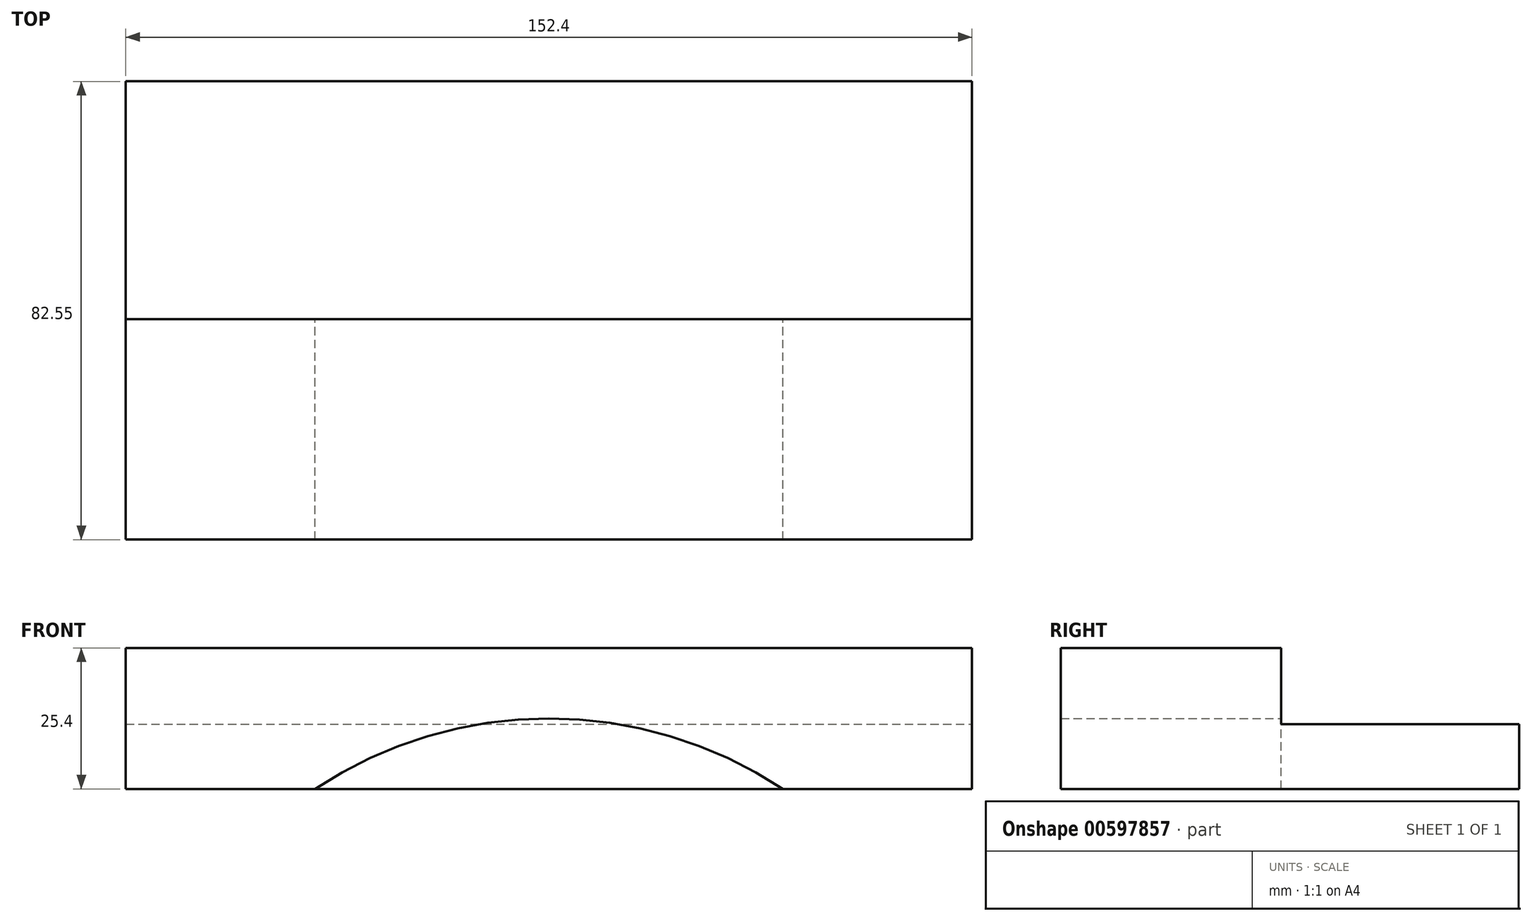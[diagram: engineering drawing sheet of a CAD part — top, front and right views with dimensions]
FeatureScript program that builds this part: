
annotation { "Feature Type Name" : "Feature", "Feature Type Description" : "" }
export const myFeature = defineFeature(function(context is Context, id is Id, definition is map)
    precondition{}
    {
        {
            var Q0;
            Q0=qCreatedBy(makeId("Front.planeOp"),FACE);
            var sketch = newSketch(context, id + "F0", { "sketchPlane" : qUnion([Q0])});
            skLineSegment(sketch, "E0.bottom", {"start": v(0, 0) * mm, "end": v(34.08, 0) * mm});
            skLineSegment(sketch, "E0.top", {"start": v(0, 25.4) * mm, "end": v(152.4, 25.4) * mm});
            skLineSegment(sketch, "E0.left", {"start": v(0, 0) * mm, "end": v(0, 25.4) * mm});
            skLineSegment(sketch, "E0.right", {"start": v(152.4, 0) * mm, "end": v(152.4, 25.4) * mm});
            skArc(sketch, "E1", {"start": v(118.32, 0) * mm, "mid": v(76.2, 12.7) * mm, "end": v(34.08, 0) * mm});
            skPoint(sketch, "E1.centerSnap0", {"position": v(76.2, 0) * mm});
            skLineSegment(sketch, "E2.trimOffspring", {"start": v(118.32, 0) * mm, "end": v(152.4, 0) * mm});
            skLineSegment(sketch, "E3", {"start": v(152.4, 12.7) * mm, "end": v(0, 12.7) * mm, "construction": true});
            skSolve(sketch);
        }
        {
            var Q0;
            Q0=qSketchRegion(id+"F0",true);
            extrude(context, id + "F1", {"entities" : qUnion([Q0]), "depth" : 39.69 * mm, "offsetDistance" : 25.4 * mm});
        }
        {
            var Q0;
            Q0=makeQuery(id+"F1.opExtrude","CAP_FACE",FACE,{"disambiguationData":[OSD([sQuery(id+"F0.wireOp",EDGE,"E0.bottom"),sQuery(id+"F0.wireOp",EDGE,"E0.top"),sQuery(id+"F0.wireOp",EDGE,"E0.left"),sQuery(id+"F0.wireOp",EDGE,"E0.right"),sQuery(id+"F0.wireOp",EDGE,"E1"),sQuery(id+"F0.wireOp",EDGE,"E2.trimOffspring")])],"isStart":true});
            var sketch = newSketch(context, id + "F2", { "sketchPlane" : qUnion([Q0])});
            skLineSegment(sketch, "E4.bottom", {"start": v(-152.4, 0) * mm, "end": v(0, 0) * mm});
            skLineSegment(sketch, "E4.top", {"start": v(-152.4, 25.4) * mm, "end": v(0, 25.4) * mm});
            skLineSegment(sketch, "E4.left", {"start": v(-152.4, 0) * mm, "end": v(-152.4, 25.4) * mm});
            skLineSegment(sketch, "E4.right", {"start": v(0, 0) * mm, "end": v(0, 25.4) * mm});
            skSolve(sketch);
        }
        {
            var Q0;
            Q0=qSketchRegion(id+"F2",true);
            extrude(context, id + "F3", {"entities" : qUnion([Q0]), "operationType" : NewBodyOperationType.ADD, "depth" : 42.86 * mm, "offsetDistance" : 25.4 * mm});
        }
        {
            var Q0;
            Q0=makeQuery(id+"F3.opExtrude","CAP_FACE",FACE,{"disambiguationData":[OSD([sQuery(id+"F2.wireOp",EDGE,"E4.bottom"),sQuery(id+"F2.wireOp",EDGE,"E4.top"),sQuery(id+"F2.wireOp",EDGE,"E4.left"),sQuery(id+"F2.wireOp",EDGE,"E4.right")])],"isStart":false});
            var sketch = newSketch(context, id + "F4", { "sketchPlane" : qUnion([Q0])});
            skLineSegment(sketch, "E5.bottom", {"start": v(0, 25.4) * mm, "end": v(-152.4, 25.4) * mm});
            skLineSegment(sketch, "E5.top", {"start": v(0, 11.68) * mm, "end": v(-152.4, 11.68) * mm});
            skLineSegment(sketch, "E5.left", {"start": v(0, 25.4) * mm, "end": v(0, 11.68) * mm});
            skLineSegment(sketch, "E5.right", {"start": v(-152.4, 25.4) * mm, "end": v(-152.4, 11.68) * mm});
            skSolve(sketch);
        }
        {
            var Q0;
            Q0=qSketchRegion(id+"F4",true);
            extrude(context, id + "F5", {"entities" : qUnion([Q0]), "operationType" : NewBodyOperationType.REMOVE, "oppositeDirection" : true, "depth" : 42.85 * mm, "offsetDistance" : 25.4 * mm});
        }
    });
